# Revit family: Door-Panel_Galaxy-Metal-Doors_Half-Glass
name_source: partatom
category: Doors
units: mm (PartAtom-declared; Revit-internal decimal feet)

## family parameters
Always vertical = Yes
Classification Number = 23.30.10.11.14
Cut with Voids When Loaded = No
Room Calculation Point = No
Shared = Yes
Work Plane-Based = No

## types (1)
- Door-Panel_Galaxy-Metal-Doors_Half-Glass
    Assembly Code = C1020110
    Construction Details = http://www.arcat.com
    Expected Lifespan (Years) = 0
    Function = Interior
    Glass Frame Width = 0' - 1"
    Glass Thickness = 0' - 0 1/4"
    Green Building-LEED = http://www.arcat.com
    Keynote = 08 11 10
    Maintenance Schedule (Months) = 0
    Manufacturer = Galaxy Metal Products, LLC
    Manufacturer Website = http://galaxymetalproducts.com
    Model = As Specified
    Product Data = http://www.arcat.com
    Rail Width Top = 0' - 6 1/8"
    Revision = R1_04-2017
    Sales Information = http://www.arcat.com
    Send Message = http://www.arcat.com
    Specification = http://www.arcat.com
    Stile Width = 0' - 6"
    URL = galaxymetalproducts.com
    Vision Lite Height = 3' - 0"
    Warranty Duration (Years) = 0

## geometry (parser evidence)
native form markers: Sweep x3
no freeform markers — native parametric forms only
